# Revit family: Door_Swing_AssaAbloy_SW200i-OHC-Double
name_source: partatom
category: Doors
units: mm (PartAtom-declared; Revit-internal decimal feet)

## family parameters
Always vertical = Yes
Classification Number = 23.30.10.17.24
Cut with Voids When Loaded = No
Host = Wall
Room Calculation Point = No
Shared = No

## types (2) — shared parameters
Assembly Code = B2030110
Construction Details = http://www.arcat.com
Description = ASSA ABLOY Low Energy Double Swing Door - Besam SW200i OHC Double Door Package as Specified
Electrical_Amperage = 20 A
Electrical_Frequency = 60 Hz
Electrical_Voltage = 120 V
Fire Rating = As Specified
Frame Depth = 0' - 4 1/2"
Function = Interior
Green Building-LEED = http://www.arcat.com
Installation-Fabrication = http://www.besam-usa.com
Jamb Width = 0' - 1 3/4"
Keynote = 08000
Manufacturer = ASSA ABLOY Entrance Systems
Manufacturer Fax = 704-290-5555
Manufacturer Website = http://www.besam-usa.com
Model = Besam SW200i OHC Double Door Package
Panel Thickness = 0' - 1 7/8"
Product Data = http://www.arcat.com
Product Properties = http://www.besam-usa.com
RO Offset = 0' - 0 1/4"
Sales Information = http://www.besam-usa.com
Send Message = http://www.arcat.com
SpecWizard = http://www.arcat.com
Specification = http://www.arcat.com
Thickness = 0' - 0"
URL = http://www.besam-usa.com
Wall Closure = By host
zero-valued in all types: Expected Lifespan (Years), Maintenance Schedule (Months), Warranty Duration (Years)

## per-type parameters (varying)
| type | Inswing | Outswing | Panic Breakout |
| Inswing with Panic Out | Yes | No | Yes |
| Outswing | No | Yes | No |

## geometry (parser evidence)
native form markers: Blend x4, Sweep x6
no freeform markers — native parametric forms only
